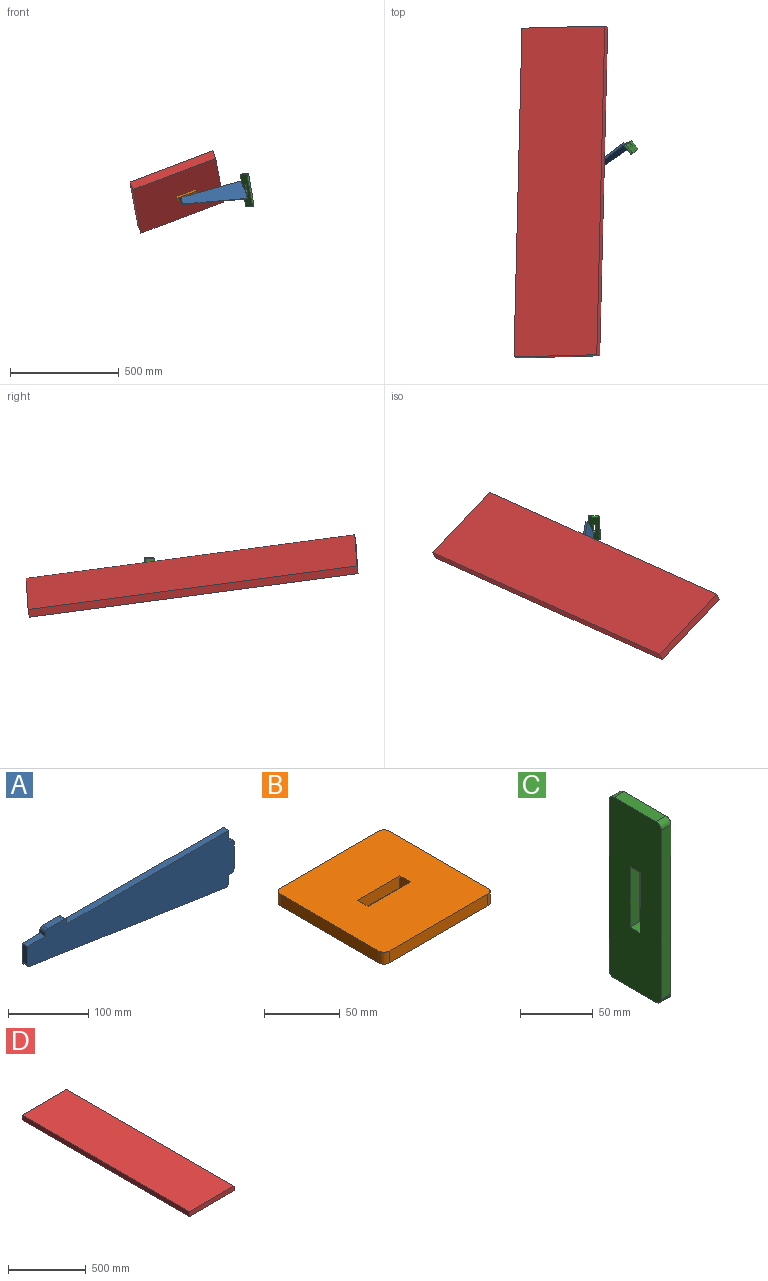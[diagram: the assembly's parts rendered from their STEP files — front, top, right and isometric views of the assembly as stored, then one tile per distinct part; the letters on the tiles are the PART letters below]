
ASSEMBLY  parts=4 mates=3
PART A: 20 faces, bbox 365.1x9.5x94.5 mm
  f0: plane 11.92x9.53mm, normal (1,0,0), area 113.6mm2, adj f1,f12,f13,f15
  f1: plane 9.53x4.76mm, normal (0,0,-1), area 45.4mm2, adj f0,f12,f13,f18
  f2: plane 41.28x9.53mm, normal (1,0,0), area 393.1mm2, adj f12,f13,f18,f19
  f3: plane 9.53x4.76mm, normal (0,0,1), area 45.4mm2, adj f4,f12,f13,f19
  f4: plane 17.46x9.53mm, normal (1,0,0), area 166.3mm2, adj f3,f5,f12,f13
  f5: plane 285.75x9.53mm, normal (0,0,1), area 2721.8mm2, adj f4,f6,f12,f13
  f6: plane 9.53x4.76mm, normal (1,0,0), area 45.4mm2, adj f5,f12,f13,f16
  f7: plane 28.58x9.53mm, normal (0,0,1), area 272.2mm2, adj f12,f13,f16,f17
  f8: plane 9.53x4.76mm, normal (-1,0,0), area 45.4mm2, adj f9,f12,f13,f17
  f9: plane 31.75x9.53mm, normal (0,0,1), area 302.4mm2, adj f8,f10,f12,f13
  f10: plane 27.66x9.53mm, normal (-1,0,0), area 263.4mm2, adj f9,f12,f13,f14
  f11: plane 346.08x52.53mm, normal (-0.15,0,-0.99), area 3334.1mm2, adj f12,f13,f14,f15
  f12: plane 365.13x94.47mm, normal (0,-1,0), area 21704.1mm2, adj f0,f1,f2,f3,f4,f5,f6,f7
  f13: plane 365.13x94.47mm, normal (0,1,0), area 21704.1mm2, adj f0,f1,f2,f3,f4,f5,f6,f7
  f14: cylinder r=4.76mm len=9.53mm, axis (0,1,0), area 64.4mm2, adj f10,f11,f12,f13
  f15: cylinder r=4.76mm len=9.53mm, axis (0,1,0), area 78.1mm2, adj f0,f11,f12,f13
  f16: cylinder r=4.76mm len=9.53mm, axis (0,-1,0), area 71.3mm2, adj f6,f7,f12,f13
  f17: cylinder r=4.76mm len=9.53mm, axis (0,1,0), area 71.3mm2, adj f7,f8,f12,f13
  f18: cylinder r=4.76mm len=9.53mm, axis (0,-1,0), area 71.3mm2, adj f1,f2,f12,f13
  f19: cylinder r=4.76mm len=9.53mm, axis (0,1,0), area 71.3mm2, adj f2,f3,f12,f13
PART B: 14 faces, bbox 101.6x101.6x9.5 mm
  f0: plane 92.08x9.53mm, normal (-1,0,0), area 877mm2, adj f8,f9,f10,f13
  f1: plane 92.08x9.53mm, normal (0,-1,0), area 877mm2, adj f8,f9,f10,f11
  f2: plane 92.08x9.53mm, normal (1,0,0), area 877mm2, adj f8,f9,f11,f12
  f3: plane 39.37x9.53mm, normal (0,-1,0), area 375mm2, adj f4,f6,f8,f9
  f4: plane 9.65x9.53mm, normal (-1,0,0), area 91.9mm2, adj f3,f5,f8,f9
  f5: plane 39.37x9.53mm, normal (0,1,0), area 375mm2, adj f4,f6,f8,f9
  f6: plane 9.65x9.53mm, normal (1,0,0), area 91.9mm2, adj f3,f5,f8,f9
  f7: plane 92.08x9.53mm, normal (0,1,0), area 877mm2, adj f8,f9,f12,f13
  f8: plane 101.6x101.6mm, normal (0,0,1), area 9923.1mm2, adj f0,f1,f2,f3,f4,f5,f6,f7
  f9: plane 101.6x101.6mm, normal (0,0,-1), area 9923.1mm2, adj f0,f1,f2,f3,f4,f5,f6,f7
  f10: cylinder r=4.76mm len=9.53mm, axis (0,0,-1), area 71.3mm2, adj f0,f1,f8,f9
  f11: cylinder r=4.76mm len=9.53mm, axis (0,0,1), area 71.3mm2, adj f1,f2,f8,f9
  f12: cylinder r=4.76mm len=9.53mm, axis (0,0,-1), area 71.3mm2, adj f2,f7,f8,f9
  f13: cylinder r=4.76mm len=9.53mm, axis (0,0,1), area 71.3mm2, adj f0,f7,f8,f9
PART C: 14 faces, bbox 9.5x50.8x152.4 mm
  f0: plane 142.24x9.53mm, normal (0,-1,0), area 1354.8mm2, adj f8,f9,f10,f13
  f1: plane 40.64x9.53mm, normal (0,0,-1), area 387.1mm2, adj f8,f9,f10,f11
  f2: plane 142.24x9.53mm, normal (0,1,0), area 1354.8mm2, adj f8,f9,f11,f12
  f3: plane 9.65x9.53mm, normal (0,0,1), area 91.9mm2, adj f4,f6,f8,f9
  f4: plane 50.93x9.53mm, normal (0,1,0), area 485.1mm2, adj f3,f5,f8,f9
  f5: plane 9.65x9.53mm, normal (0,0,-1), area 91.9mm2, adj f4,f6,f8,f9
  f6: plane 50.93x9.53mm, normal (0,-1,0), area 485.1mm2, adj f3,f5,f8,f9
  f7: plane 40.64x9.53mm, normal (0,0,1), area 387.1mm2, adj f8,f9,f12,f13
  f8: plane 152.4x50.8mm, normal (1,0,0), area 7228.2mm2, adj f0,f1,f2,f3,f4,f5,f6,f7
  f9: plane 152.4x50.8mm, normal (-1,0,0), area 7228.2mm2, adj f0,f1,f2,f3,f4,f5,f6,f7
  f10: cylinder r=5.08mm len=9.53mm, axis (-1,0,0), area 76mm2, adj f0,f1,f8,f9
  f11: cylinder r=5.08mm len=9.53mm, axis (1,0,0), area 76mm2, adj f1,f2,f8,f9
  f12: cylinder r=5.08mm len=9.53mm, axis (-1,0,0), area 76mm2, adj f2,f7,f8,f9
  f13: cylinder r=5.08mm len=9.53mm, axis (1,0,0), area 76mm2, adj f0,f7,f8,f9
PART D: 6 faces, bbox 406.4x1524x38.1 mm
  f0: plane 1524x38.1mm, normal (-1,0,0), area 58064.4mm2, adj f1,f3,f4,f5
  f1: plane 406.4x38.1mm, normal (0,-1,0), area 15483.8mm2, adj f0,f2,f4,f5
  f2: plane 1524x38.1mm, normal (1,0,0), area 58064.4mm2, adj f1,f3,f4,f5
  f3: plane 406.4x38.1mm, normal (0,1,0), area 15483.8mm2, adj f0,f2,f4,f5
  f4: plane 1524x406.4mm, normal (0,0,1), area 619353.6mm2, adj f0,f1,f2,f3
  f5: plane 1524x406.4mm, normal (0,0,-1), area 619353.6mm2, adj f0,f1,f2,f3
PLACE A rot(axis=(-0.33,-0.43,0.84),41.3deg) t=(123.58,135.89,95.69)mm
PLACE B rot(axis=(-0.35,-0.94,-0.01),22.1deg) t=(46.67,-121,102.85)mm
PLACE C rot(axis=(0.1,-0.3,0.95),39deg) t=(1.1,276.42,155.37)mm
PLACE D rot(axis=(-0.35,-0.94,0),22.1deg) t=(-930.21,-472.51,-208.35)mm
MATE planar D.f5 <-> B.f8  axis (0.35,-0.13,-0.93) through (-159.52,-93.27,30.83)mm
MATE pin_slot A.f2 <-> C.f8  axis (0.78,0.59,0.21) through (146.1,135.88,58)mm
MATE pin_slot A.f7 <-> B.f8  axis (-0.35,0.13,0.93) through (-114.92,-46.19,41.12)mm
